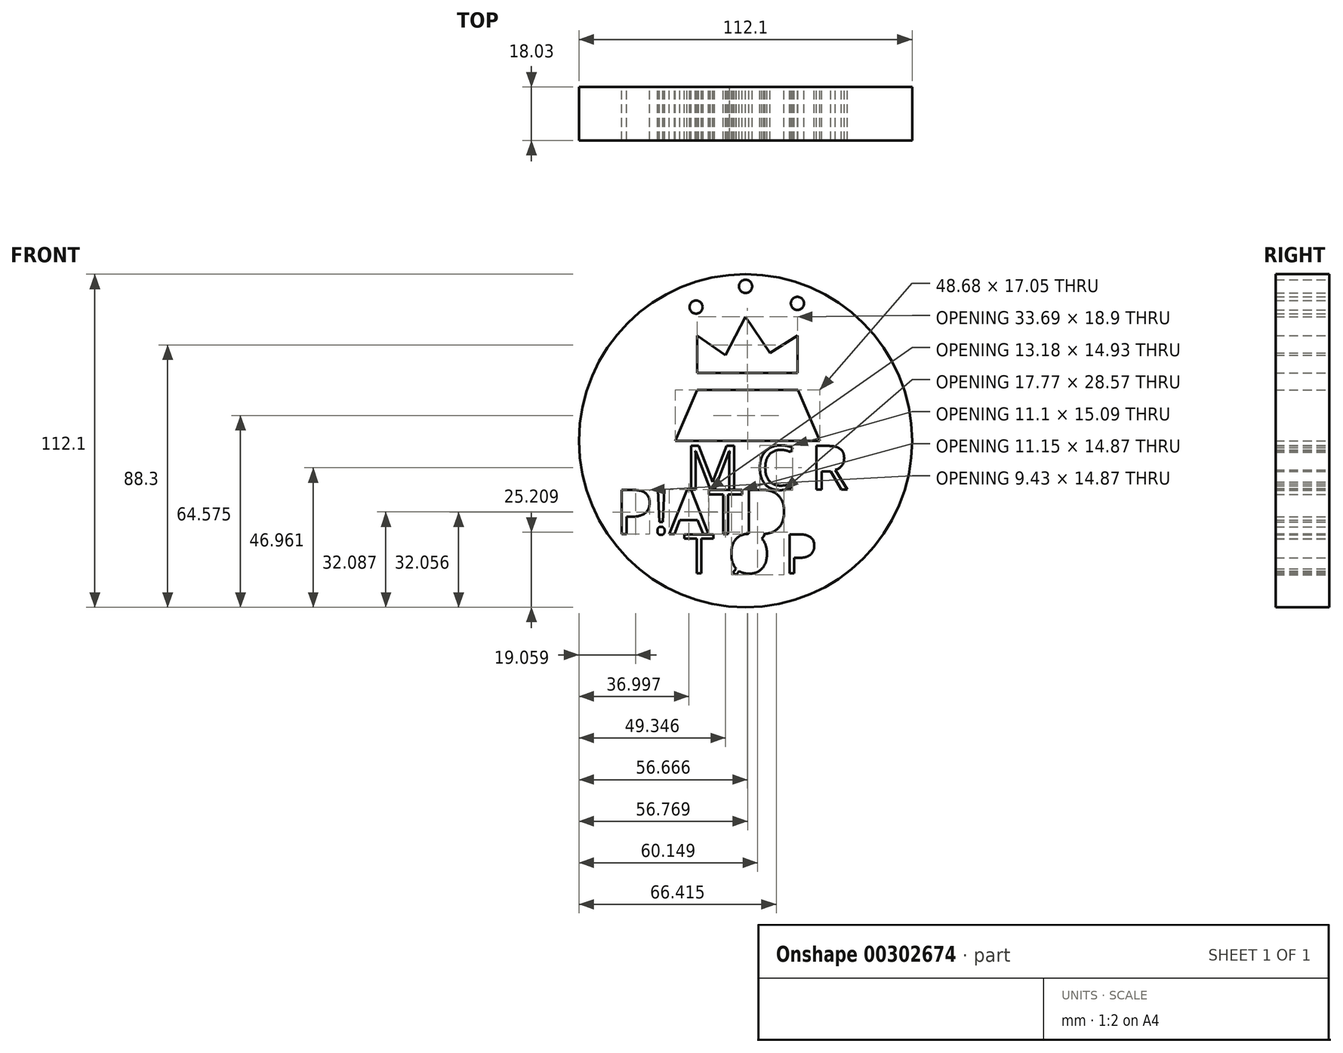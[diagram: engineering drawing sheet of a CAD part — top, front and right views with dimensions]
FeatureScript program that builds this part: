
annotation { "Feature Type Name" : "Feature", "Feature Type Description" : "" }
export const myFeature = defineFeature(function(context is Context, id is Id, definition is map)
    precondition{}
    {
        {
            var Q0;
            Q0=qCreatedBy(makeId("Front.planeOp"),FACE);
            var sketch = newSketch(context, id + "F0", { "sketchPlane" : qUnion([Q0])});
            skCircle(sketch, "E0", {"center": v(0, 0) * mm, "radius": 56.05 * mm});
            skLineSegment(sketch, "E1", {"start": v(17.67, 17.05) * mm, "end": v(-16.23, 17.05) * mm});
            skPoint(sketch, "E2.end.orphan", {"position": v(17.67, 0) * mm});
            skLineSegment(sketch, "E3", {"start": v(-16.23, 0) * mm, "end": v(-23.62, 0) * mm});
            skLineSegment(sketch, "E4", {"start": v(17.67, 0) * mm, "end": v(25.06, 0) * mm});
            skLineSegment(sketch, "E5", {"start": v(-16.23, 17.05) * mm, "end": v(-23.62, 0) * mm});
            skLineSegment(sketch, "E6", {"start": v(17.67, 17.05) * mm, "end": v(25.06, 0) * mm});
            skLineSegment(sketch, "E7", {"start": v(-16.23, 0) * mm, "end": v(17.67, 0) * mm});
            skLineSegment(sketch, "E8", {"start": v(-16.23, 22.8) * mm, "end": v(17.46, 22.8) * mm});
            skLineSegment(sketch, "E9", {"start": v(-16.23, 22.8) * mm, "end": v(-16.23, 35.33) * mm});
            skLineSegment(sketch, "E10", {"start": v(17.46, 22.8) * mm, "end": v(17.46, 35.33) * mm});
            skLineSegment(sketch, "E11", {"start": v(-16.23, 35.33) * mm, "end": v(-6.78, 28.76) * mm});
            skLineSegment(sketch, "E12", {"start": v(17.46, 35.33) * mm, "end": v(8.22, 29.58) * mm});
            skLineSegment(sketch, "E13", {"start": v(-6.78, 28.76) * mm, "end": v(0, 41.7) * mm});
            skLineSegment(sketch, "E14", {"start": v(0, 41.7) * mm, "end": v(8.22, 29.58) * mm});
            skCircle(sketch, "E15", {"center": v(-16.64, 44.99) * mm, "radius": 2.21 * mm});
            skCircle(sketch, "E16", {"center": v(0, 51.97) * mm, "radius": 2.22 * mm});
            skCircle(sketch, "E17", {"center": v(17.46, 46.22) * mm, "radius": 2.21 * mm});
            skText(sketch, "E18", { "text": "F O B", "fontName": "OpenSans-Regular.ttf"});
            skText(sketch, "E19", { "text": "P!ATD", "fontName": "OpenSans-Regular.ttf"});
            skText(sketch, "E20", { "text": "M C R", "fontName": "OpenSans-Regular.ttf"});
            skText(sketch, "E21", { "text": "T Ø P", "fontName": "OpenSans-Regular.ttf"});
            const initialGuessF0  = {"E18": [-0.0152, 0.0041, 1, 0, 0.00945], "E19": [-0.04375, -0.03143, 1, 0, 0.015], "E20": [-0.02034, -0.01643, 1, 0, 0.0148], "E21": [-0.02075, -0.04458, 1, 0, 0.01315]};
            skSetInitialGuess(sketch, initialGuessF0);
            skSolve(sketch);
        }
        {
            var Q0;
            Q0 = qSketchRegion(id + "F0", true);
            var Q1;
            Q1=makeQuery(id+"F0.imprint","IMPRINT",FACE,{"disambiguationData":[TD([[makeQuery(id+"F0.imprint","IMPRINT",EDGE,{"derivedFrom":sQuery(id+"F0.wireOp",EDGE,"E0")}),1.0]])]});
            extrude(context, id + "F1", {"entities" : qUnion([Q0, Q1]), "depth" : 18.03 * mm});
        }
    });
